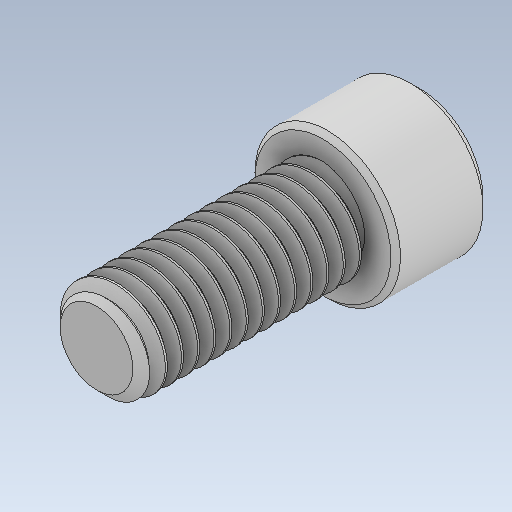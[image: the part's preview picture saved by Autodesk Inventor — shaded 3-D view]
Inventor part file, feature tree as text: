
AUTODESK INVENTOR PART (.ipt)
format: ipt  version: 2021 (Build 250183000, 183)  size: 596,480 bytes
history: native  units: in
note: dims shown in document units (in); Inventor stores cm internally (conversion verified against a paired STEP export)
features: chamfer x1
ambient origin geometry x8: Origin, YZ Plane, XZ Plane, XY Plane, X Axis, Y Axis, Z Axis, Center Point
bodies: Solid1 (feature_tree)
feature tree (1):
  chamfer  "Chamfer2"  [1 undecoded]
note: 1 required parameter value undecoded (feature->parameter linkage not recoverable at this tier; creation-order binding heuristic only, values carry confidence <= 0.55)
